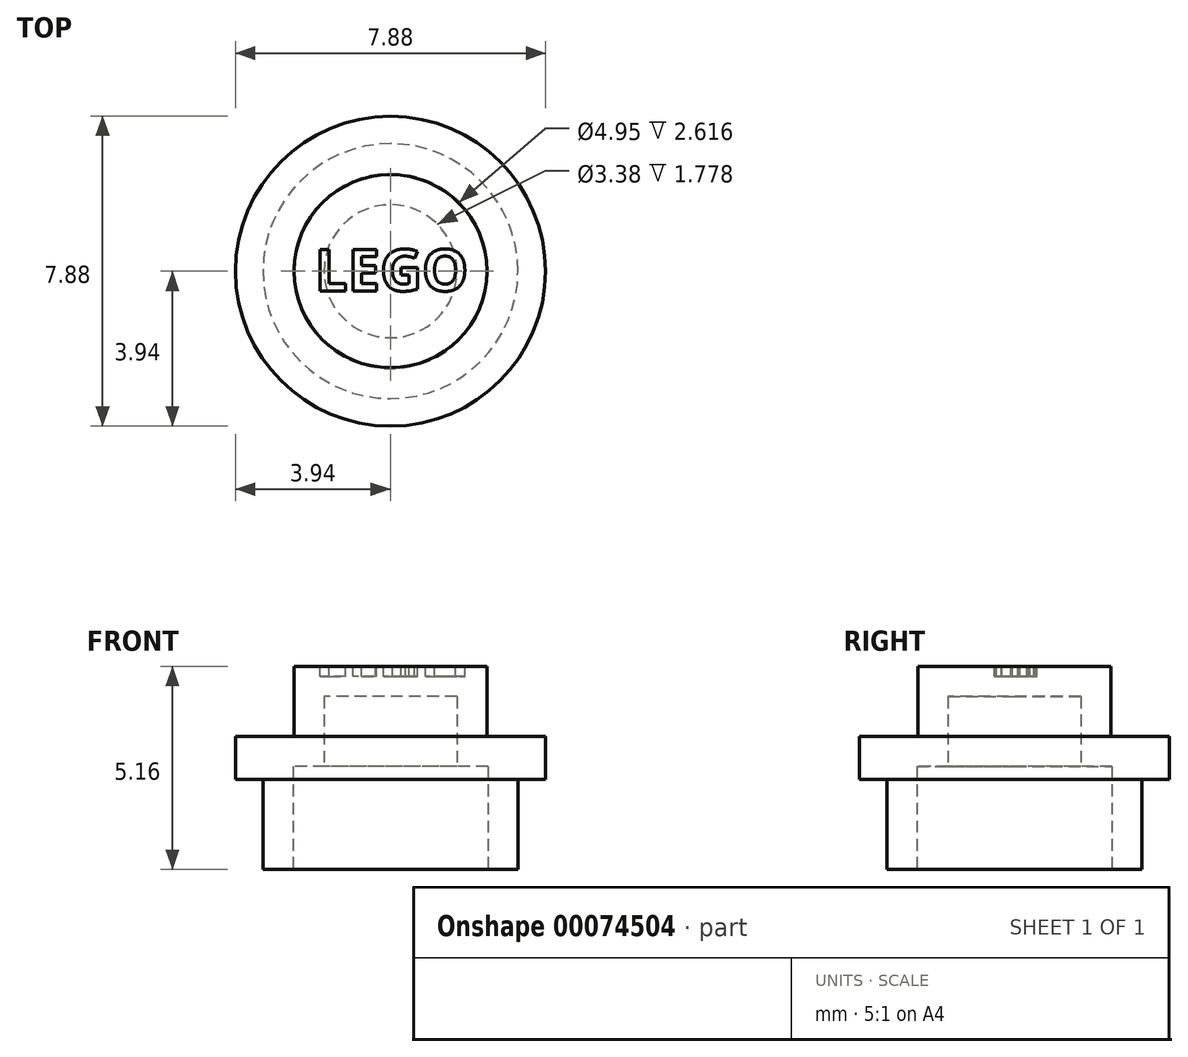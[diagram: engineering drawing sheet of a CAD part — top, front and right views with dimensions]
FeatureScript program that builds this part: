
annotation { "Feature Type Name" : "Feature", "Feature Type Description" : "" }
export const myFeature = defineFeature(function(context is Context, id is Id, definition is map)
    precondition{}
    {
        {
            var Q0;
            Q0=qCreatedBy(makeId("Top.planeOp"),FACE);
            var sketch = newSketch(context, id + "F0", { "sketchPlane" : qUnion([Q0])});
            skCircle(sketch, "E0", {"center": v(0, 0) * mm, "radius": 3.24 * mm});
            skSolve(sketch);
        }
        {
            var Q0;
            Q0 = qSketchRegion(id + "F0", true);
            extrude(context, id + "F1", {"entities" : qUnion([Q0]), "depth" : 2.3 * mm});
        }
        {
            var Q0;
            Q0=makeQuery(id+"F1.opExtrude","CAP_FACE",FACE,{"disambiguationData":[OSD([sQuery(id+"F0.wireOp",EDGE,"E0")])],"isStart":false});
            var sketch = newSketch(context, id + "F2", { "sketchPlane" : qUnion([Q0])});
            skCircle(sketch, "E1", {"center": v(0, 0) * mm, "radius": 3.94 * mm});
            skSolve(sketch);
        }
        {
            var Q0;
            Q0 = qSketchRegion(id + "F2", true);
            extrude(context, id + "F3", {"entities" : qUnion([Q0]), "operationType" : NewBodyOperationType.ADD, "depth" : 1.1 * mm});
        }
        {
            var Q0;
            Q0=makeQuery(id+"F3.opExtrude","CAP_FACE",FACE,{"disambiguationData":[OSD([sQuery(id+"F2.wireOp",EDGE,"E1")])],"isStart":false});
            var sketch = newSketch(context, id + "F4", { "sketchPlane" : qUnion([Q0])});
            skCircle(sketch, "E2", {"center": v(0, 0) * mm, "radius": 2.45 * mm});
            skSolve(sketch);
        }
        {
            var Q0;
            Q0 = qSketchRegion(id + "F4", true);
            extrude(context, id + "F5", {"entities" : qUnion([Q0]), "operationType" : NewBodyOperationType.ADD, "depth" : 1.78 * mm});
        }
        {
            var Q0;
            Q0=makeQuery(id+"F1.opExtrude","CAP_FACE",FACE,{"disambiguationData":[OSD([sQuery(id+"F0.wireOp",EDGE,"E0")])],"isStart":true});
            shell(context, id + "F6", {"entities" : qUnion([Q0]), "thickness" : 0.76 * mm});
        }
        {
            var Q0;
            Q0=makeQuery(id+"F5.opExtrude","CAP_FACE",FACE,{"disambiguationData":[OSD([sQuery(id+"F4.wireOp",EDGE,"E2")])],"isStart":false});
            var sketch = newSketch(context, id + "F7", { "sketchPlane" : qUnion([Q0])});
            skText(sketch, "E3", { "text": "LEGO", "fontName": "OpenSans-Bold.ttf"});
            const initialGuessF7  = {"E3": [-0.00192, -0.0005, 1, 0, 0.00106]};
            skSetInitialGuess(sketch, initialGuessF7);
            skSolve(sketch);
        }
        {
            var Q0;
            Q0 = qSketchRegion(id + "F7", true);
            extrude(context, id + "F8", {"entities" : qUnion([Q0]), "operationType" : NewBodyOperationType.REMOVE, "oppositeDirection" : true, "depth" : 0.25 * mm});
        }
    });
